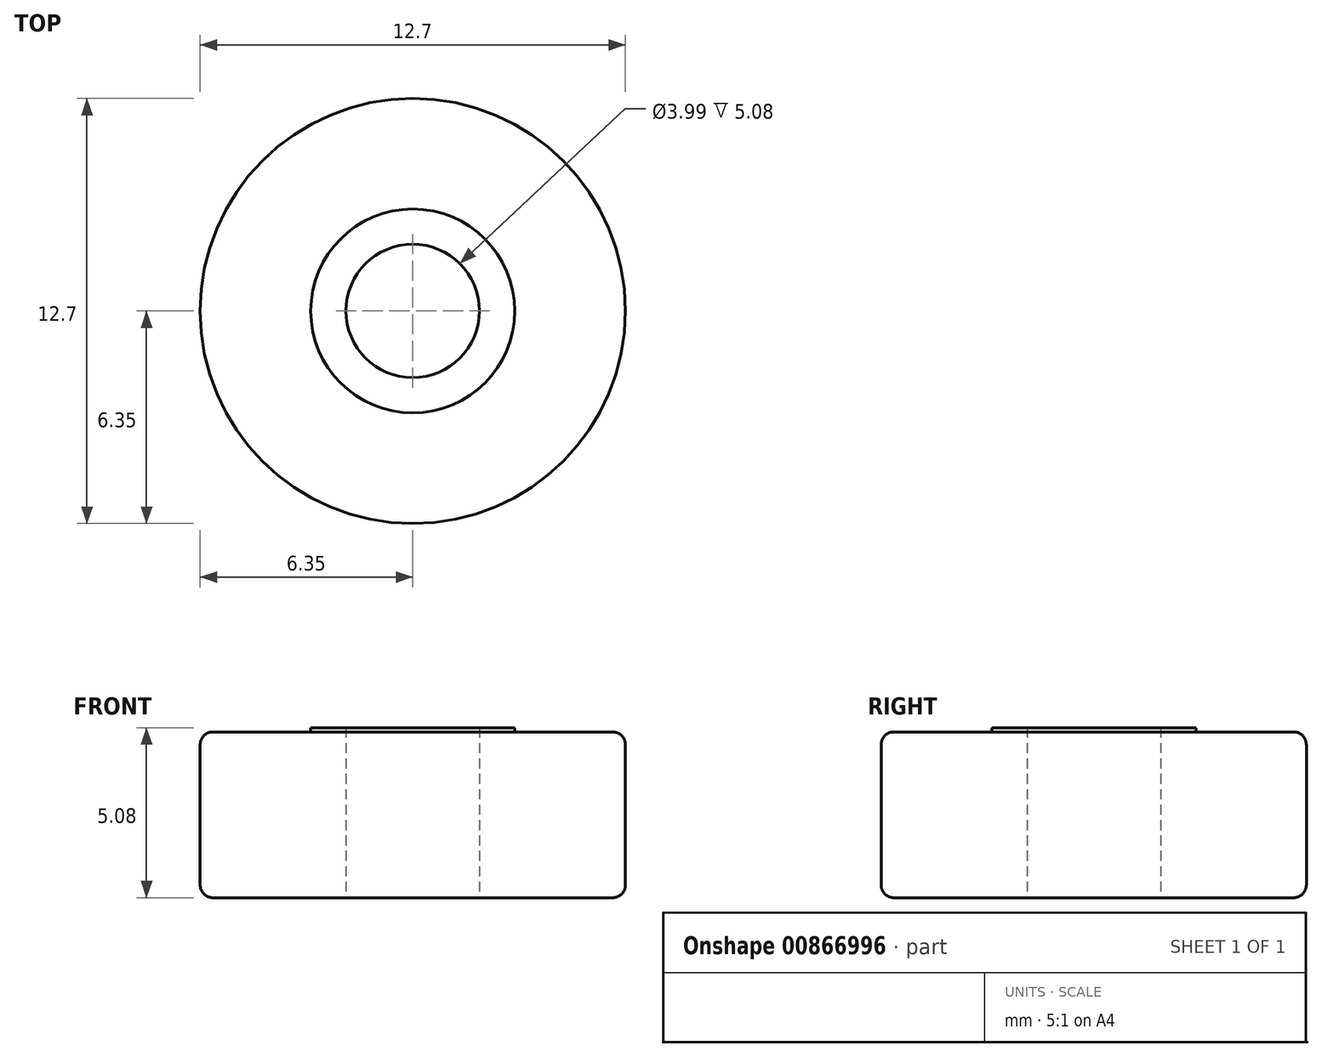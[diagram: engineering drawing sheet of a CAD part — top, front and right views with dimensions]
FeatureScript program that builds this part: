
annotation { "Feature Type Name" : "Feature", "Feature Type Description" : "" }
export const myFeature = defineFeature(function(context is Context, id is Id, definition is map)
    precondition{}
    {
        {
            var Q0;
            Q0=qCreatedBy(makeId("Top.planeOp"),FACE);
            var sketch = newSketch(context, id + "F0", { "sketchPlane" : qUnion([Q0])});
            skCircle(sketch, "E0", {"center": v(0, 0) * mm, "radius": 6.35 * mm});
            skCircle(sketch, "E1", {"center": v(0, 0) * mm, "radius": 2 * mm});
            skSolve(sketch);
        }
        {
            var Q0;
            Q0=makeQuery(id+"F0.imprint","IMPRINT",FACE,{"disambiguationData":[TD([[makeQuery(id+"F0.imprint","IMPRINT",EDGE,{"derivedFrom":sQuery(id+"F0.wireOp",EDGE,"E0")}),1.0]])]});
            extrude(context, id + "F1", {"entities" : qUnion([Q0]), "depth" : 4.95 * mm, "offsetDistance" : 25.4 * mm});
        }
        {
            var Q0;
            Q0=makeQuery(id+"F1.opExtrude","CAP_FACE",FACE,{"disambiguationData":[OSD([sQuery(id+"F0.wireOp",EDGE,"E0"),sQuery(id+"F0.wireOp",EDGE,"E1")])],"isStart":false});
            var sketch = newSketch(context, id + "F2", { "sketchPlane" : qUnion([Q0])});
            skCircle(sketch, "E2", {"center": v(0, 0) * mm, "radius": 3.05 * mm});
            skSolve(sketch);
        }
        {
            var Q0;
            Q0=makeQuery(id+"F2.imprint","IMPRINT",FACE,{"disambiguationData":[TD([[makeQuery(id+"F2.imprint","IMPRINT",EDGE,{"derivedFrom":sQuery(id+"F2.wireOp",EDGE,"E2")}),1.0]])]});
            extrude(context, id + "F3", {"entities" : qUnion([Q0]), "operationType" : NewBodyOperationType.ADD, "depth" : 0.13 * mm, "offsetDistance" : 25.4 * mm});
        }
        {
            var Q0;
            Q0=makeQuery(id+"F1.opExtrude","CAP_EDGE",EDGE,{"disambiguationData":[OSD([sQuery(id+"F0.wireOp",EDGE,"E0")])],"isStart":false});
            var Q1;
            Q1=makeQuery(id+"F1.opExtrude","CAP_EDGE",EDGE,{"disambiguationData":[OSD([sQuery(id+"F0.wireOp",EDGE,"E0")])],"isStart":true});
            fillet(context, id + "F4", {"entities" : qUnion([Q0, Q1]), "radius" : 0.38 * mm, "tangentPropagation" : true, "allowEdgeOverflow" : false});
        }
    });
